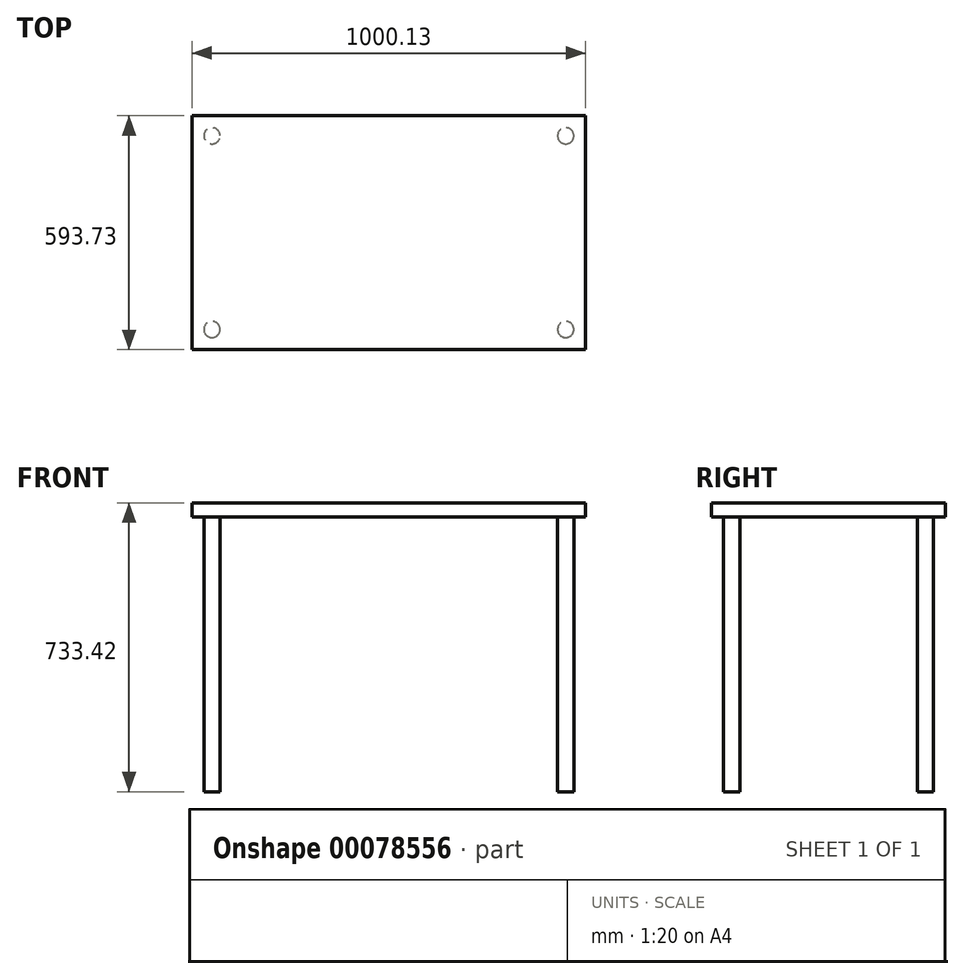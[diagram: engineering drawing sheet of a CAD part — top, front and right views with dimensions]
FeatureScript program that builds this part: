
annotation { "Feature Type Name" : "Feature", "Feature Type Description" : "" }
export const myFeature = defineFeature(function(context is Context, id is Id, definition is map)
    precondition{}
    {
        {
            var Q0;
            Q0=qCreatedBy(makeId("Top.planeOp"),FACE);
            var sketch = newSketch(context, id + "F0", { "sketchPlane" : qUnion([Q0])});
            skLineSegment(sketch, "E0.bottom", {"start": v(629.7, -474.96) * mm, "end": v(-370.43, -474.96) * mm});
            skLineSegment(sketch, "E0.top", {"start": v(629.7, 118.77) * mm, "end": v(-370.43, 118.77) * mm});
            skLineSegment(sketch, "E0.left", {"start": v(629.7, -474.96) * mm, "end": v(629.7, 118.77) * mm});
            skLineSegment(sketch, "E0.right", {"start": v(-370.43, -474.96) * mm, "end": v(-370.43, 118.77) * mm});
            skSolve(sketch);
        }
        {
            var Q0;
            Q0=makeQuery(id+"F0.imprint","IMPRINT",FACE,{"disambiguationData":[TD([[makeQuery(id+"F0.imprint","IMPRINT",EDGE,{"derivedFrom":sQuery(id+"F0.wireOp",EDGE,"E0.bottom")}),-1.0]])]});
            extrude(context, id + "F1", {"entities" : qUnion([Q0]), "depth" : 34.92 * mm});
        }
        {
            var Q0;
            Q0=makeQuery(id+"F1.opExtrude","CAP_FACE",FACE,{"disambiguationData":[OSD([sQuery(id+"F0.wireOp",EDGE,"E0.bottom"),sQuery(id+"F0.wireOp",EDGE,"E0.top"),sQuery(id+"F0.wireOp",EDGE,"E0.left"),sQuery(id+"F0.wireOp",EDGE,"E0.right")])],"isStart":true});
            var sketch = newSketch(context, id + "F2", { "sketchPlane" : qUnion([Q0])});
            skCircle(sketch, "E1", {"center": v(-319.63, -67.97) * mm, "radius": 20.64 * mm});
            skCircle(sketch, "E2", {"center": v(-319.63, 424.16) * mm, "radius": 20.64 * mm});
            skCircle(sketch, "E3", {"center": v(578.9, -67.97) * mm, "radius": 20.64 * mm});
            skCircle(sketch, "E4", {"center": v(578.9, 424.16) * mm, "radius": 20.64 * mm});
            skSolve(sketch);
        }
        {
            var Q0;
            Q0=makeQuery(id+"F2.imprint","IMPRINT",FACE,{"disambiguationData":[TD([[makeQuery(id+"F2.imprint","IMPRINT",EDGE,{"derivedFrom":sQuery(id+"F2.wireOp",EDGE,"E3")}),1.0]])]});
            var Q1;
            Q1=makeQuery(id+"F2.imprint","IMPRINT",FACE,{"disambiguationData":[TD([[makeQuery(id+"F2.imprint","IMPRINT",EDGE,{"derivedFrom":sQuery(id+"F2.wireOp",EDGE,"E1")}),1.0]])]});
            var Q2;
            Q2=makeQuery(id+"F2.imprint","IMPRINT",FACE,{"disambiguationData":[TD([[makeQuery(id+"F2.imprint","IMPRINT",EDGE,{"derivedFrom":sQuery(id+"F2.wireOp",EDGE,"E2")}),1.0]])]});
            var Q3;
            Q3=makeQuery(id+"F2.imprint","IMPRINT",FACE,{"disambiguationData":[TD([[makeQuery(id+"F2.imprint","IMPRINT",EDGE,{"derivedFrom":sQuery(id+"F2.wireOp",EDGE,"E4")}),1.0]])]});
            extrude(context, id + "F3", {"entities" : qUnion([Q0, Q1, Q2, Q3]), "operationType" : NewBodyOperationType.ADD, "depth" : 698.5 * mm});
        }
    });
